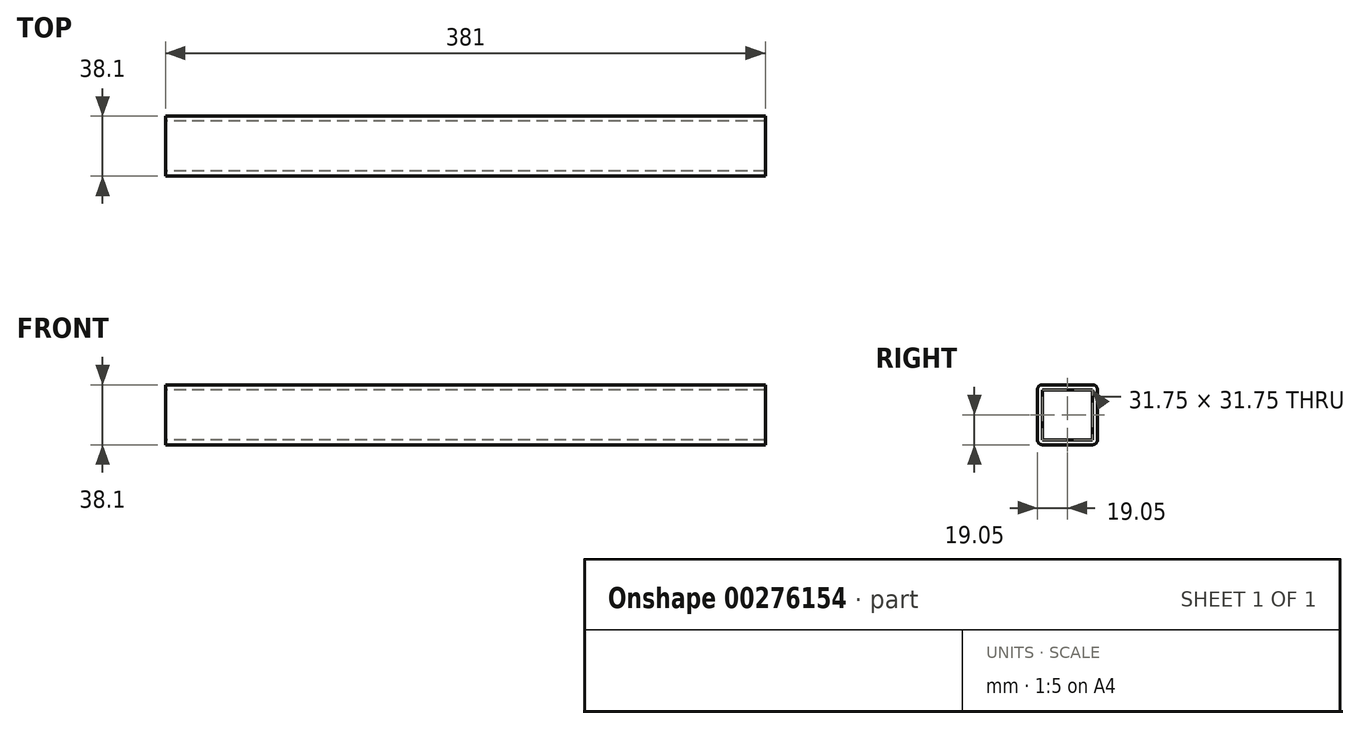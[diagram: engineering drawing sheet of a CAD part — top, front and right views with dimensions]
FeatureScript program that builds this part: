
annotation { "Feature Type Name" : "Feature", "Feature Type Description" : "" }
export const myFeature = defineFeature(function(context is Context, id is Id, definition is map)
    precondition{}
    {
        {
            var Q0;
            Q0=qCreatedBy(makeId("Right.planeOp"),FACE);
            var sketch = newSketch(context, id + "F0", { "sketchPlane" : qUnion([Q0])});
            skLineSegment(sketch, "E0.bottom", {"start": v(19.05, 19.05) * mm, "end": v(-19.05, 19.05) * mm});
            skLineSegment(sketch, "E0.top", {"start": v(19.05, -19.05) * mm, "end": v(-19.05, -19.05) * mm});
            skLineSegment(sketch, "E0.left", {"start": v(19.05, 19.05) * mm, "end": v(19.05, -19.05) * mm});
            skLineSegment(sketch, "E0.right", {"start": v(-19.05, 19.05) * mm, "end": v(-19.05, -19.05) * mm});
            skPoint(sketch, "E0.middle", {"position": v(0, 0) * mm});
            skSolve(sketch);
        }
        {
            var Q0;
            Q0 = qSketchRegion(id + "F0", true);
            extrude(context, id + "F1", {"entities" : qUnion([Q0]), "depth" : 381 * mm});
        }
        {
            var Q0;
            Q0=makeQuery(id+"F1.opExtrude","CAP_FACE",FACE,{"disambiguationData":[OSD([sQuery(id+"F0.wireOp",EDGE,"E0.bottom"),sQuery(id+"F0.wireOp",EDGE,"E0.top"),sQuery(id+"F0.wireOp",EDGE,"E0.left"),sQuery(id+"F0.wireOp",EDGE,"E0.right")])],"isStart":false});
            var Q1;
            Q1=makeQuery(id+"F1.opExtrude","CAP_FACE",FACE,{"disambiguationData":[OSD([sQuery(id+"F0.wireOp",EDGE,"E0.bottom"),sQuery(id+"F0.wireOp",EDGE,"E0.top"),sQuery(id+"F0.wireOp",EDGE,"E0.left"),sQuery(id+"F0.wireOp",EDGE,"E0.right")])],"isStart":true});
            shell(context, id + "F2", {"entities" : qUnion([Q0, Q1]), "thickness" : 3.17 * mm});
        }
        {
            var Q0;
            Q0=makeQuery(id+"F1.opExtrude","SWEPT_EDGE",EDGE,{"disambiguationData":[OSD([sQuery(id+"F0.wireOp",EDGE,"E0.bottom"),sQuery(id+"F0.wireOp",EDGE,"E0.right")])]});
            var Q1;
            Q1=makeQuery(id+"F1.opExtrude","SWEPT_EDGE",EDGE,{"disambiguationData":[OSD([sQuery(id+"F0.wireOp",EDGE,"E0.bottom"),sQuery(id+"F0.wireOp",EDGE,"E0.left")])]});
            var Q2;
            Q2=makeQuery(id+"F1.opExtrude","SWEPT_EDGE",EDGE,{"disambiguationData":[OSD([sQuery(id+"F0.wireOp",EDGE,"E0.top"),sQuery(id+"F0.wireOp",EDGE,"E0.right")])]});
            var Q3;
            Q3=makeQuery(id+"F1.opExtrude","SWEPT_EDGE",EDGE,{"disambiguationData":[OSD([sQuery(id+"F0.wireOp",EDGE,"E0.top"),sQuery(id+"F0.wireOp",EDGE,"E0.left")])]});
            fillet(context, id + "F3", {"entities" : qUnion([Q0, Q1, Q2, Q3]), "radius" : 3.17 * mm, "tangentPropagation" : true, "allowEdgeOverflow" : false});
        }
    });
